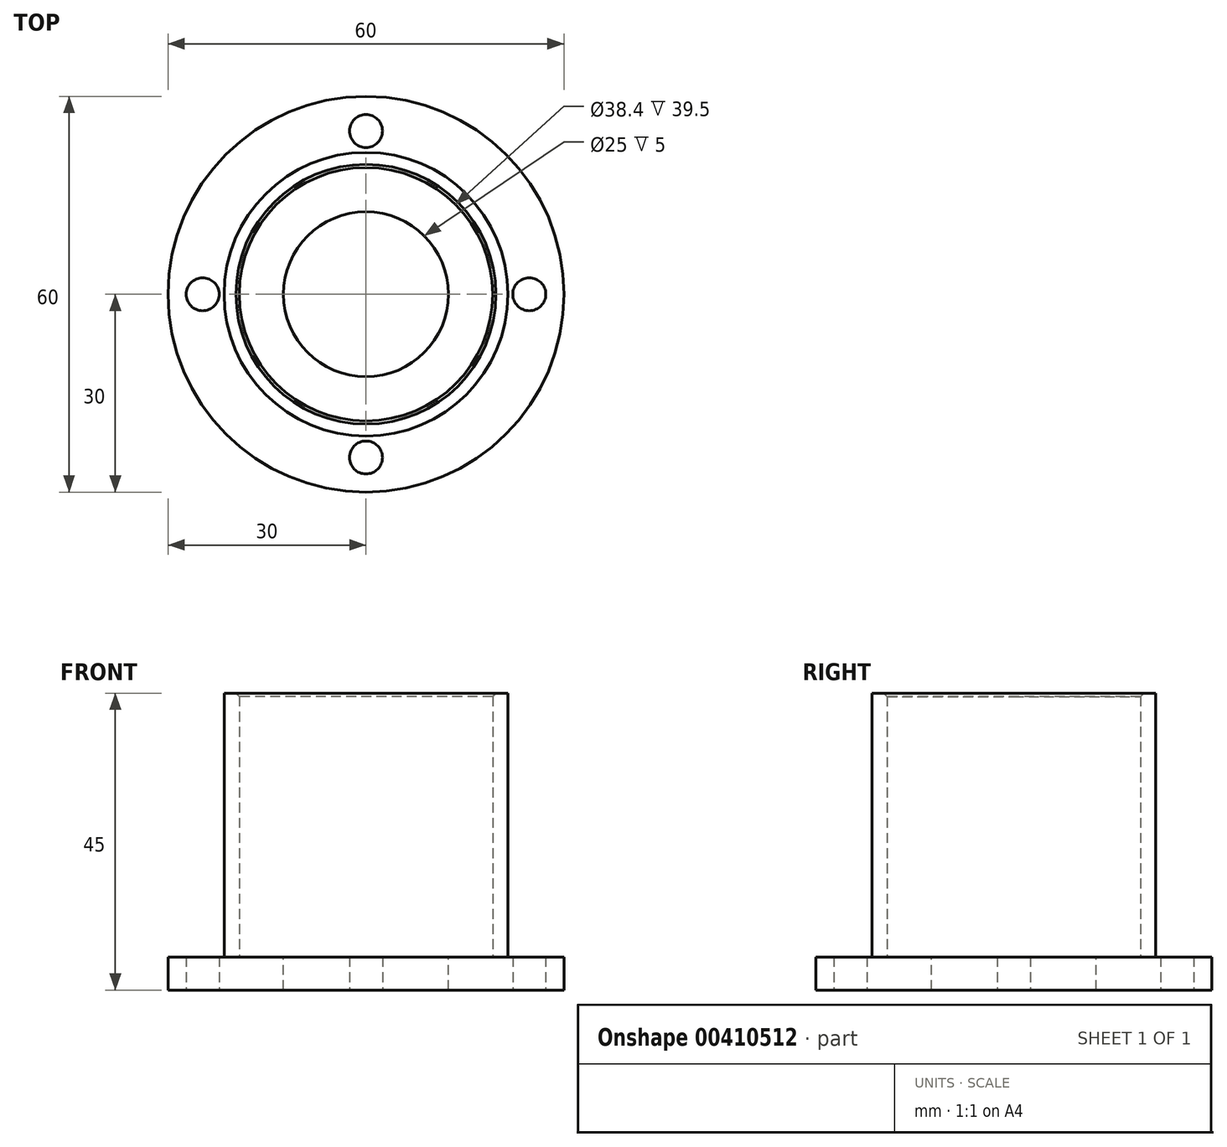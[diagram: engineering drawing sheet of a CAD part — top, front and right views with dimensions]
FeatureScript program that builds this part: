
annotation { "Feature Type Name" : "Feature", "Feature Type Description" : "" }
export const myFeature = defineFeature(function(context is Context, id is Id, definition is map)
    precondition{}
    {
        {
            var Q0;
            Q0=qCreatedBy(makeId("Top.planeOp"),FACE);
            var sketch = newSketch(context, id + "F0", { "sketchPlane" : qUnion([Q0])});
            skCircle(sketch, "E0", {"center": v(0, 0) * mm, "radius": 19.2 * mm});
            skCircle(sketch, "E1", {"center": v(0, 0) * mm, "radius": 21.5 * mm});
            skSolve(sketch);
        }
        {
            var Q0;
            Q0=makeQuery(id+"F0.imprint","IMPRINT",FACE,{"disambiguationData":[TD([[makeQuery(id+"F0.imprint","IMPRINT",EDGE,{"derivedFrom":sQuery(id+"F0.wireOp",EDGE,"E0")}),-1.0]])]});
            extrude(context, id + "F1", {"entities" : qUnion([Q0]), "depth" : 40 * mm});
        }
        {
            var Q0;
            Q0=qCreatedBy(makeId("Top.planeOp"),FACE);
            var sketch = newSketch(context, id + "F2", { "sketchPlane" : qUnion([Q0])});
            skCircle(sketch, "E2", {"center": v(0, 0) * mm, "radius": 12.5 * mm});
            skCircle(sketch, "E3", {"center": v(0, 0) * mm, "radius": 30 * mm});
            skSolve(sketch);
        }
        {
            var Q0;
            Q0=makeQuery(id+"F2.imprint","IMPRINT",FACE,{"disambiguationData":[TD([[makeQuery(id+"F2.imprint","IMPRINT",EDGE,{"derivedFrom":sQuery(id+"F2.wireOp",EDGE,"E2")}),-1.0]])]});
            extrude(context, id + "F3", {"entities" : qUnion([Q0]), "operationType" : NewBodyOperationType.ADD, "oppositeDirection" : true, "depth" : 5 * mm});
        }
        {
            var Q0;
            Q0=makeQuery(id+"F3.opExtrude","CAP_FACE",FACE,{"disambiguationData":[OSD([sQuery(id+"F2.wireOp",EDGE,"E2"),sQuery(id+"F2.wireOp",EDGE,"E3")])],"isStart":false});
            var sketch = newSketch(context, id + "F4", { "sketchPlane" : qUnion([Q0])});
            skPoint(sketch, "E4", {"position": v(24.75, 0) * mm});
            skPoint(sketch, "E5.1.0", {"position": v(0, 24.75) * mm});
            skPoint(sketch, "E5.2.0", {"position": v(-24.75, 0) * mm});
            skPoint(sketch, "E5.3.0", {"position": v(0, -24.75) * mm});
            skPoint(sketch, "E5.center", {"position": v(0, 0) * mm});
            skSolve(sketch);
        }
        {
            var Q0;
            Q0=sQuery(id+"F4.wireOp",VERTEX,"E5.2.0");
            var Q1;
            Q1=sQuery(id+"F4.wireOp",VERTEX,"E5.1.0");
            var Q2;
            Q2=sQuery(id+"F4.wireOp",VERTEX,"E4");
            var Q3;
            Q3=sQuery(id+"F4.wireOp",VERTEX,"E5.3.0");
            var Q4;
            Q4=makeQuery(id+"F1.opExtrude","SWEPT_BODY",BODY,{"disambiguationData":[OSD([sQuery(id+"F0.wireOp",EDGE,"E0"),sQuery(id+"F0.wireOp",EDGE,"E1")])]});
            hole(context, id + "F5", {"style" : HoleStyle.SIMPLE, "endStyle" : HoleEndStyle.THROUGH, "holeDiameter" : 5 * mm, "isTappedThrough" : true, "tappedDepth" : 12 * mm, "tapClearance" : 3, "locations" : qUnion([Q0, Q1, Q2, Q3]), "scope" : qUnion([Q4])});
        }
        {
            var Q0;
            Q0=makeQuery(id+"F1.opExtrude","CAP_EDGE",EDGE,{"disambiguationData":[OSD([sQuery(id+"F0.wireOp",EDGE,"E0")])],"isStart":false});
            chamfer(context, id + "F6", {"entities" : qUnion([Q0]), "width" : 0.5 * mm, "tangentPropagation" : true});
        }
    });
